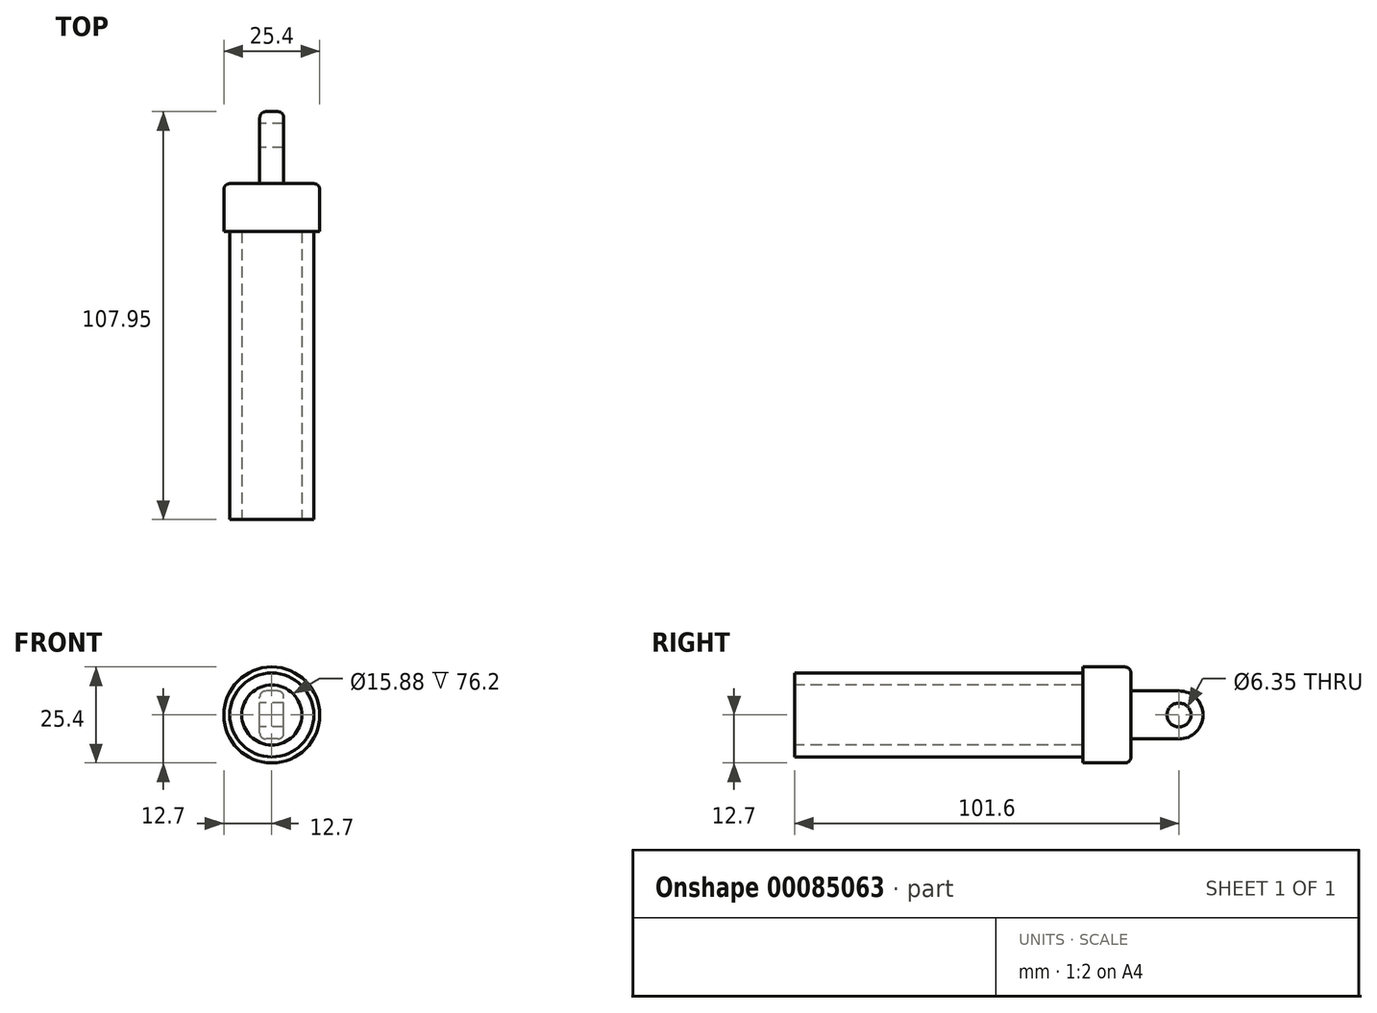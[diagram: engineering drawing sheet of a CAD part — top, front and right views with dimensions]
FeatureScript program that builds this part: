
annotation { "Feature Type Name" : "Feature", "Feature Type Description" : "" }
export const myFeature = defineFeature(function(context is Context, id is Id, definition is map)
    precondition{}
    {
        {
            var Q0;
            Q0=qCreatedBy(makeId("Front.planeOp"),FACE);
            var sketch = newSketch(context, id + "F0", { "sketchPlane" : qUnion([Q0])});
            skCircle(sketch, "E0", {"center": v(0, 0) * mm, "radius": 12.7 * mm});
            skSolve(sketch);
        }
        {
            var Q0;
            Q0 = qSketchRegion(id + "F0", true);
            extrude(context, id + "F1", {"entities" : qUnion([Q0]), "depth" : 12.7 * mm});
        }
        {
            var Q0;
            Q0=qCreatedBy(makeId("Right.planeOp"),FACE);
            var sketch = newSketch(context, id + "F2", { "sketchPlane" : qUnion([Q0])});
            skLineSegment(sketch, "E1.0", {"start": v(-12.7, -12.7) * mm, "end": v(-12.7, 12.7) * mm});
            skLineSegment(sketch, "E2.0", {"start": v(0, -12.7) * mm, "end": v(0, 12.7) * mm});
            skLineSegment(sketch, "E3.bottom", {"start": v(0, 6.35) * mm, "end": v(12.7, 6.35) * mm});
            skLineSegment(sketch, "E3.top", {"start": v(0, -6.35) * mm, "end": v(12.7, -6.35) * mm});
            skLineSegment(sketch, "E3.left", {"start": v(0, 6.35) * mm, "end": v(0, -6.35) * mm});
            skLineSegment(sketch, "E3.right", {"start": v(12.7, 6.35) * mm, "end": v(12.7, -6.35) * mm});
            skLineSegment(sketch, "E4", {"start": v(0, 0) * mm, "end": v(72.07, 0) * mm, "construction": true});
            skCircle(sketch, "E5", {"center": v(12.7, 0) * mm, "radius": 6.35 * mm});
            skCircle(sketch, "E6", {"center": v(12.7, 0) * mm, "radius": 3.18 * mm});
            skSolve(sketch);
        }
        {
            var Q0;
            {var subQ0=sQuery(id+"F2.wireOp",EDGE,"E3.bottom");Q0=makeQuery(id+"F2.imprint","IMPRINT",FACE,{"disambiguationData":[TD([[makeQuery(id+"F2.imprint","IMPRINT",EDGE,{"derivedFrom":subQ0}),-1.0]])]});}
            var Q1;
            {var subQ1=sQuery(id+"F2.wireOp",EDGE,"E3.right");var subQ3=sQuery(id+"F2.wireOp",EDGE,"E6");var subQ4=makeQuery(id+"F2.imprint","INTERSECT",VERTEX,{"disambiguationData":[OD(0.0)],"derivedFrom":[subQ1,subQ3]});Q1=makeQuery(id+"F2.imprint","IMPRINT",FACE,{"disambiguationData":[TD([[makeQuery(id+"F2.imprint","IMPRINT",EDGE,{"disambiguationData":[TD([[subQ4,-1.0]])],"derivedFrom":subQ3}),-1.0]])]});}
            var Q2;
            {var subQ1=sQuery(id+"F2.wireOp",EDGE,"E3.right");var subQ3=sQuery(id+"F2.wireOp",EDGE,"E6");var subQ4=makeQuery(id+"F2.imprint","INTERSECT",VERTEX,{"disambiguationData":[OD(0.0)],"derivedFrom":[subQ1,subQ3]});Q2=makeQuery(id+"F2.imprint","IMPRINT",FACE,{"disambiguationData":[TD([[makeQuery(id+"F2.imprint","IMPRINT",EDGE,{"disambiguationData":[TD([[subQ4,1.0]])],"derivedFrom":subQ3}),-1.0]])]});}
            extrude(context, id + "F3", {"entities" : qUnion([Q0, Q1, Q2]), "operationType" : NewBodyOperationType.ADD, "endBound" : BoundingType.SYMMETRIC, "depth" : 6.35 * mm});
        }
        {
            var Q0;
            Q0=makeQuery(id+"F1.opExtrude","CAP_EDGE",EDGE,{"disambiguationData":[OSD([sQuery(id+"F0.wireOp",EDGE,"E0")])],"isStart":true});
            var Q1;
            Q1=makeQuery(id+"F3.opExtrude","CAP_EDGE",EDGE,{"disambiguationData":[OSD([sQuery(id+"F2.wireOp",EDGE,"E3.left")])],"isStart":true});
            var Q2;
            Q2=makeQuery(id+"F3.opExtrude","SWEPT_EDGE",EDGE,{"disambiguationData":[OSD([sQuery(id+"F2.wireOp",EDGE,"E3.bottom"),sQuery(id+"F2.wireOp",EDGE,"E3.left")])]});
            var Q3;
            Q3=makeQuery(id+"F3.opExtrude","CAP_EDGE",EDGE,{"disambiguationData":[OSD([sQuery(id+"F2.wireOp",EDGE,"E3.bottom")])],"isStart":false});
            var Q4;
            Q4=makeQuery(id+"F3.opExtrude","CAP_EDGE",EDGE,{"disambiguationData":[OSD([sQuery(id+"F2.wireOp",EDGE,"E3.bottom")])],"isStart":true});
            fillet(context, id + "F4", {"entities" : qUnion([Q0, Q1, Q2, Q3, Q4]), "radius" : 1.59 * mm, "tangentPropagation" : true, "allowEdgeOverflow" : false});
        }
        {
            var Q0;
            Q0=makeQuery(id+"F1.opExtrude","CAP_FACE",FACE,{"disambiguationData":[OSD([sQuery(id+"F0.wireOp",EDGE,"E0")])],"isStart":false});
            var sketch = newSketch(context, id + "F5", { "sketchPlane" : qUnion([Q0])});
            skCircle(sketch, "E7.0", {"center": v(0, 0) * mm, "radius": 12.7 * mm});
            skCircle(sketch, "E8", {"center": v(0, 0) * mm, "radius": 11.11 * mm});
            skSolve(sketch);
        }
        {
            var Q0;
            Q0=makeQuery(id+"F5.imprint","IMPRINT",FACE,{"disambiguationData":[TD([[makeQuery(id+"F5.imprint","IMPRINT",EDGE,{"derivedFrom":sQuery(id+"F5.wireOp",EDGE,"E8")}),1.0]])]});
            extrude(context, id + "F6", {"entities" : qUnion([Q0]), "depth" : 76.2 * mm});
        }
        {
            var Q0;
            Q0=makeQuery(id+"F6.opExtrude","CAP_FACE",FACE,{"disambiguationData":[OSD([sQuery(id+"F5.wireOp",EDGE,"E8")])],"isStart":false});
            var sketch = newSketch(context, id + "F7", { "sketchPlane" : qUnion([Q0])});
            skPoint(sketch, "E9.0", {"position": v(0, 0) * mm});
            skCircle(sketch, "E10", {"center": v(0, 0) * mm, "radius": 7.94 * mm});
            skCircle(sketch, "E11.0", {"center": v(0, 0) * mm, "radius": 11.11 * mm});
            skSolve(sketch);
        }
        {
            var Q0;
            Q0=makeQuery(id+"F7.imprint","IMPRINT",FACE,{"disambiguationData":[TD([[makeQuery(id+"F7.imprint","IMPRINT",EDGE,{"derivedFrom":sQuery(id+"F7.wireOp",EDGE,"E10")}),1.0]])]});
            extrude(context, id + "F8", {"entities" : qUnion([Q0]), "operationType" : NewBodyOperationType.REMOVE, "oppositeDirection" : true, "depth" : 76.2 * mm});
        }
    });
